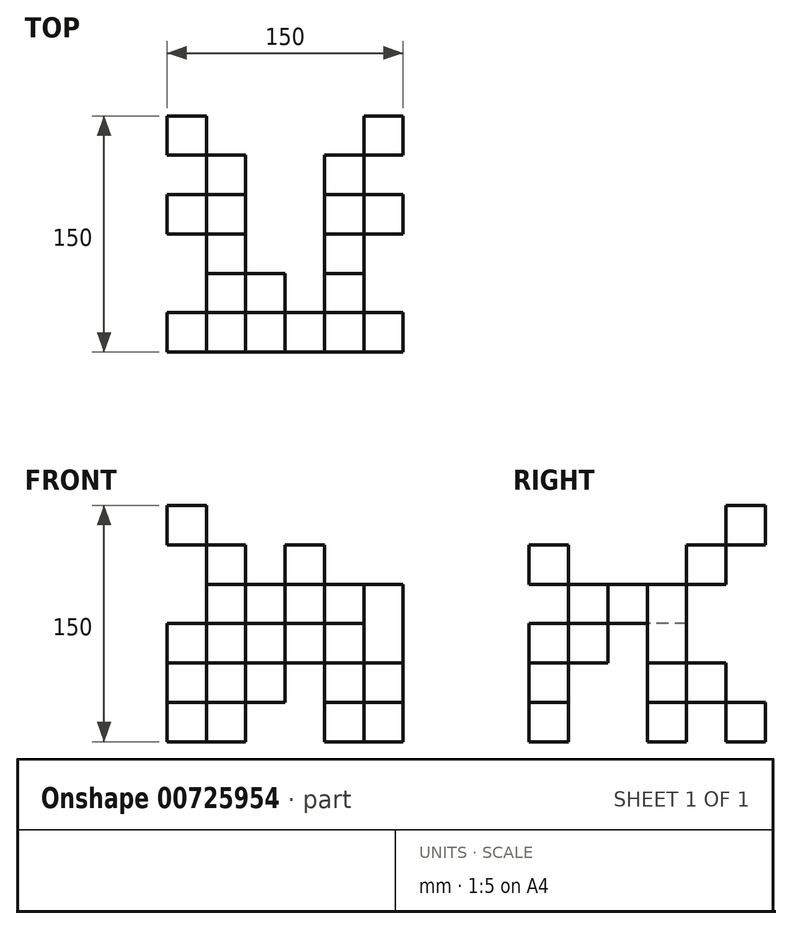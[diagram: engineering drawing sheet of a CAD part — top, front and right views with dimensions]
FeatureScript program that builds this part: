
annotation { "Feature Type Name" : "Feature", "Feature Type Description" : "" }
export const myFeature = defineFeature(function(context is Context, id is Id, definition is map)
    precondition{}
    {
        {
            var Q0;
            Q0=qCreatedBy(makeId("Right.planeOp"),FACE);
            cPlane(context, id + "F0", {"entities" : qUnion([Q0]), "cplaneType" : CPlaneType.OFFSET, "offset" : 25 * mm, "width" : 150 * mm, "height" : 150 * mm});
        }
        {
            var Q0;
            Q0=qCreatedBy(makeId("Right.planeOp"),FACE);
            cPlane(context, id + "F1", {"entities" : qUnion([Q0]), "cplaneType" : CPlaneType.OFFSET, "offset" : 25 * mm, "oppositeDirection" : true, "width" : 150 * mm, "height" : 150 * mm});
        }
        {
            var Q0;
            Q0=qCreatedBy(id+"F1.planeOp",FACE);
            cPlane(context, id + "F2", {"entities" : qUnion([Q0]), "cplaneType" : CPlaneType.OFFSET, "offset" : 25 * mm, "oppositeDirection" : true, "width" : 150 * mm, "height" : 150 * mm});
        }
        {
            var Q0;
            Q0=qCreatedBy(id+"F2.planeOp",FACE);
            cPlane(context, id + "F3", {"entities" : qUnion([Q0]), "cplaneType" : CPlaneType.OFFSET, "offset" : 25 * mm, "oppositeDirection" : true, "width" : 150 * mm, "height" : 150 * mm});
        }
        {
            var Q0;
            Q0=qCreatedBy(makeId("Front.planeOp"),FACE);
            cPlane(context, id + "F4", {"entities" : qUnion([Q0]), "cplaneType" : CPlaneType.OFFSET, "offset" : 25 * mm, "width" : 150 * mm, "height" : 150 * mm});
        }
        {
            var Q0;
            Q0=qCreatedBy(id+"F4.planeOp",FACE);
            cPlane(context, id + "F5", {"entities" : qUnion([Q0]), "cplaneType" : CPlaneType.OFFSET, "offset" : 25 * mm, "width" : 150 * mm, "height" : 150 * mm});
        }
        {
            var Q0;
            Q0=qCreatedBy(makeId("Front.planeOp"),FACE);
            cPlane(context, id + "F6", {"entities" : qUnion([Q0]), "cplaneType" : CPlaneType.OFFSET, "offset" : 25 * mm, "oppositeDirection" : true, "width" : 150 * mm, "height" : 150 * mm});
        }
        {
            var Q0;
            Q0=qCreatedBy(id+"F6.planeOp",FACE);
            cPlane(context, id + "F7", {"entities" : qUnion([Q0]), "cplaneType" : CPlaneType.OFFSET, "offset" : 25 * mm, "oppositeDirection" : true, "width" : 150 * mm, "height" : 150 * mm});
        }
        {
            var Q0;
            Q0=qCreatedBy(makeId("Top.planeOp"),FACE);
            cPlane(context, id + "F8", {"entities" : qUnion([Q0]), "cplaneType" : CPlaneType.OFFSET, "offset" : 25 * mm, "width" : 150 * mm, "height" : 150 * mm});
        }
        {
            var Q0;
            Q0=qCreatedBy(id+"F8.planeOp",FACE);
            cPlane(context, id + "F9", {"entities" : qUnion([Q0]), "cplaneType" : CPlaneType.OFFSET, "offset" : 25 * mm, "width" : 150 * mm, "height" : 150 * mm});
        }
        {
            var Q0;
            Q0=qCreatedBy(makeId("Top.planeOp"),FACE);
            cPlane(context, id + "F10", {"entities" : qUnion([Q0]), "cplaneType" : CPlaneType.OFFSET, "offset" : 25 * mm, "oppositeDirection" : true, "width" : 150 * mm, "height" : 150 * mm});
        }
        {
            var Q0;
            Q0=qCreatedBy(id+"F10.planeOp",FACE);
            cPlane(context, id + "F11", {"entities" : qUnion([Q0]), "cplaneType" : CPlaneType.OFFSET, "offset" : 25 * mm, "oppositeDirection" : true, "width" : 150 * mm, "height" : 150 * mm});
        }
        {
            var Q0;
            Q0=qCreatedBy(id+"F3.planeOp",FACE);
            var sketch = newSketch(context, id + "F12", { "sketchPlane" : qUnion([Q0])});
            skLineSegment(sketch, "E0.bottom", {"start": v(75, -75) * mm, "end": v(50, -75) * mm});
            skLineSegment(sketch, "E0.top", {"start": v(75, -50) * mm, "end": v(50, -50) * mm});
            skLineSegment(sketch, "E0.left", {"start": v(75, -75) * mm, "end": v(75, -50) * mm});
            skLineSegment(sketch, "E0.right", {"start": v(50, -75) * mm, "end": v(50, -50) * mm});
            skSolve(sketch);
        }
        {
            var Q0;
            Q0 = qSketchRegion(id + "F12", true);
            extrude(context, id + "F13", {"entities" : qUnion([Q0]), "depth" : 25 * mm, "offsetDistance" : 25 * mm});
        }
        {
            var Q0;
            Q0=makeQuery(id+"F13.opExtrude","SWEPT_BODY",BODY,{"disambiguationData":[OSD([sQuery(id+"F12.wireOp",EDGE,"E0.bottom"),sQuery(id+"F12.wireOp",EDGE,"E0.top"),sQuery(id+"F12.wireOp",EDGE,"E0.left"),sQuery(id+"F12.wireOp",EDGE,"E0.right")])]});
            transform(context, id + "F14", {"entities" : qUnion([Q0]), "transformType" : TransformType.COPY});
        }
        {
            var Q0;
            Q0=makeQuery(id+"F14.opPattern","COPY",BODY,{"derivedFrom":makeQuery(id+"F13.opExtrude","SWEPT_BODY",BODY,{"disambiguationData":[OSD([sQuery(id+"F12.wireOp",EDGE,"E0.bottom"),sQuery(id+"F12.wireOp",EDGE,"E0.top"),sQuery(id+"F12.wireOp",EDGE,"E0.left"),sQuery(id+"F12.wireOp",EDGE,"E0.right")])]}),"instanceName":"1"});
            transform(context, id + "F15", {"entities" : qUnion([Q0]), "transformType" : TransformType.TRANSLATION_3D, "dx" : 0 * mm, "dy" : -25 * mm, "dz" : 25 * mm, "makeCopy" : true});
        }
        {
            var Q0;
            Q0=makeQuery(id+"F15.opPattern","COPY",BODY,{"derivedFrom":makeQuery(id+"F14.opPattern","COPY",BODY,{"derivedFrom":makeQuery(id+"F13.opExtrude","SWEPT_BODY",BODY,{"disambiguationData":[OSD([sQuery(id+"F12.wireOp",EDGE,"E0.bottom"),sQuery(id+"F12.wireOp",EDGE,"E0.top"),sQuery(id+"F12.wireOp",EDGE,"E0.left"),sQuery(id+"F12.wireOp",EDGE,"E0.right")])]}),"instanceName":"1"}),"instanceName":"1"});
            transform(context, id + "F16", {"entities" : qUnion([Q0]), "transformType" : TransformType.TRANSLATION_3D, "dx" : 0 * mm, "dy" : -25 * mm, "dz" : 25 * mm, "makeCopy" : true});
        }
        {
            var Q0;
            Q0=makeQuery(id+"F15.opPattern","COPY",BODY,{"derivedFrom":makeQuery(id+"F14.opPattern","COPY",BODY,{"derivedFrom":makeQuery(id+"F13.opExtrude","SWEPT_BODY",BODY,{"disambiguationData":[OSD([sQuery(id+"F12.wireOp",EDGE,"E0.bottom"),sQuery(id+"F12.wireOp",EDGE,"E0.top"),sQuery(id+"F12.wireOp",EDGE,"E0.left"),sQuery(id+"F12.wireOp",EDGE,"E0.right")])]}),"instanceName":"1"}),"instanceName":"1"});
            transform(context, id + "F17", {"entities" : qUnion([Q0]), "transformType" : TransformType.TRANSLATION_3D, "dx" : 25 * mm, "dy" : 0 * mm, "dz" : 0 * mm, "makeCopy" : false});
        }
        {
            var Q0;
            Q0=makeQuery(id+"F13.opExtrude","SWEPT_BODY",BODY,{"disambiguationData":[OSD([sQuery(id+"F12.wireOp",EDGE,"E0.bottom"),sQuery(id+"F12.wireOp",EDGE,"E0.top"),sQuery(id+"F12.wireOp",EDGE,"E0.left"),sQuery(id+"F12.wireOp",EDGE,"E0.right")])]});
            var Q1;
            Q1=makeQuery(id+"F16.opPattern","COPY",BODY,{"derivedFrom":makeQuery(id+"F15.opPattern","COPY",BODY,{"derivedFrom":makeQuery(id+"F14.opPattern","COPY",BODY,{"derivedFrom":makeQuery(id+"F13.opExtrude","SWEPT_BODY",BODY,{"disambiguationData":[OSD([sQuery(id+"F12.wireOp",EDGE,"E0.bottom"),sQuery(id+"F12.wireOp",EDGE,"E0.top"),sQuery(id+"F12.wireOp",EDGE,"E0.left"),sQuery(id+"F12.wireOp",EDGE,"E0.right")])]}),"instanceName":"1"}),"instanceName":"1"}),"instanceName":"1"});
            var Q2;
            Q2=makeQuery(id+"F15.opPattern","COPY",BODY,{"derivedFrom":makeQuery(id+"F14.opPattern","COPY",BODY,{"derivedFrom":makeQuery(id+"F13.opExtrude","SWEPT_BODY",BODY,{"disambiguationData":[OSD([sQuery(id+"F12.wireOp",EDGE,"E0.bottom"),sQuery(id+"F12.wireOp",EDGE,"E0.top"),sQuery(id+"F12.wireOp",EDGE,"E0.left"),sQuery(id+"F12.wireOp",EDGE,"E0.right")])]}),"instanceName":"1"}),"instanceName":"1"});
            var Q3;
            Q3=makeQuery(id+"F14.opPattern","COPY",BODY,{"derivedFrom":makeQuery(id+"F13.opExtrude","SWEPT_BODY",BODY,{"disambiguationData":[OSD([sQuery(id+"F12.wireOp",EDGE,"E0.bottom"),sQuery(id+"F12.wireOp",EDGE,"E0.top"),sQuery(id+"F12.wireOp",EDGE,"E0.left"),sQuery(id+"F12.wireOp",EDGE,"E0.right")])]}),"instanceName":"1"});
            var Q4;
            Q4=qCreatedBy(makeId("Front.planeOp"),FACE);
            mirror(context, id + "F18", {"entities" : qUnion([Q0, Q1, Q2, Q3]), "mirrorPlane" : qUnion([Q4])});
        }
        {
            var Q0;
            Q0=makeQuery(id+"F18.opPattern","COPY",BODY,{"derivedFrom":makeQuery(id+"F16.opPattern","COPY",BODY,{"derivedFrom":makeQuery(id+"F15.opPattern","COPY",BODY,{"derivedFrom":makeQuery(id+"F14.opPattern","COPY",BODY,{"derivedFrom":makeQuery(id+"F13.opExtrude","SWEPT_BODY",BODY,{"disambiguationData":[OSD([sQuery(id+"F12.wireOp",EDGE,"E0.bottom"),sQuery(id+"F12.wireOp",EDGE,"E0.top"),sQuery(id+"F12.wireOp",EDGE,"E0.left"),sQuery(id+"F12.wireOp",EDGE,"E0.right")])]}),"instanceName":"1"}),"instanceName":"1"}),"instanceName":"1"}),"instanceName":"1"});
            transform(context, id + "F19", {"entities" : qUnion([Q0]), "transformType" : TransformType.TRANSLATION_3D, "dx" : 0 * mm, "dy" : 0 * mm, "dz" : 25 * mm, "makeCopy" : false});
        }
        {
            var Q0;
            Q0=makeQuery(id+"F18.opPattern","COPY",BODY,{"derivedFrom":makeQuery(id+"F16.opPattern","COPY",BODY,{"derivedFrom":makeQuery(id+"F15.opPattern","COPY",BODY,{"derivedFrom":makeQuery(id+"F14.opPattern","COPY",BODY,{"derivedFrom":makeQuery(id+"F13.opExtrude","SWEPT_BODY",BODY,{"disambiguationData":[OSD([sQuery(id+"F12.wireOp",EDGE,"E0.bottom"),sQuery(id+"F12.wireOp",EDGE,"E0.top"),sQuery(id+"F12.wireOp",EDGE,"E0.left"),sQuery(id+"F12.wireOp",EDGE,"E0.right")])]}),"instanceName":"1"}),"instanceName":"1"}),"instanceName":"1"}),"instanceName":"1"});
            transform(context, id + "F20", {"entities" : qUnion([Q0]), "transformType" : TransformType.TRANSLATION_3D, "dx" : 25 * mm, "dy" : 0 * mm, "dz" : 0 * mm, "makeCopy" : false});
        }
        {
            var Q0;
            Q0=makeQuery(id+"F18.opPattern","COPY",BODY,{"derivedFrom":makeQuery(id+"F15.opPattern","COPY",BODY,{"derivedFrom":makeQuery(id+"F14.opPattern","COPY",BODY,{"derivedFrom":makeQuery(id+"F13.opExtrude","SWEPT_BODY",BODY,{"disambiguationData":[OSD([sQuery(id+"F12.wireOp",EDGE,"E0.bottom"),sQuery(id+"F12.wireOp",EDGE,"E0.top"),sQuery(id+"F12.wireOp",EDGE,"E0.left"),sQuery(id+"F12.wireOp",EDGE,"E0.right")])]}),"instanceName":"1"}),"instanceName":"1"}),"instanceName":"1"});
            var Q1;
            Q1=makeQuery(id+"F18.opPattern","COPY",BODY,{"derivedFrom":makeQuery(id+"F13.opExtrude","SWEPT_BODY",BODY,{"disambiguationData":[OSD([sQuery(id+"F12.wireOp",EDGE,"E0.bottom"),sQuery(id+"F12.wireOp",EDGE,"E0.top"),sQuery(id+"F12.wireOp",EDGE,"E0.left"),sQuery(id+"F12.wireOp",EDGE,"E0.right")])]}),"instanceName":"1"});
            transform(context, id + "F21", {"entities" : qUnion([Q0, Q1]), "transformType" : TransformType.TRANSLATION_3D, "dx" : 0 * mm, "dy" : 0 * mm, "dz" : 25 * mm, "makeCopy" : false});
        }
        {
            var Q0;
            Q0=makeQuery(id+"F18.opPattern","COPY",BODY,{"derivedFrom":makeQuery(id+"F14.opPattern","COPY",BODY,{"derivedFrom":makeQuery(id+"F13.opExtrude","SWEPT_BODY",BODY,{"disambiguationData":[OSD([sQuery(id+"F12.wireOp",EDGE,"E0.bottom"),sQuery(id+"F12.wireOp",EDGE,"E0.top"),sQuery(id+"F12.wireOp",EDGE,"E0.left"),sQuery(id+"F12.wireOp",EDGE,"E0.right")])]}),"instanceName":"1"}),"instanceName":"1"});
            transform(context, id + "F22", {"entities" : qUnion([Q0]), "transformType" : TransformType.TRANSLATION_3D, "dx" : 25 * mm, "dy" : 0 * mm, "dz" : 0 * mm, "makeCopy" : false});
        }
        {
            var Q0;
            Q0=makeQuery(id+"F13.opExtrude","SWEPT_BODY",BODY,{"disambiguationData":[OSD([sQuery(id+"F12.wireOp",EDGE,"E0.bottom"),sQuery(id+"F12.wireOp",EDGE,"E0.top"),sQuery(id+"F12.wireOp",EDGE,"E0.left"),sQuery(id+"F12.wireOp",EDGE,"E0.right")])]});
            var Q1;
            Q1=makeQuery(id+"F18.opPattern","COPY",BODY,{"derivedFrom":makeQuery(id+"F16.opPattern","COPY",BODY,{"derivedFrom":makeQuery(id+"F15.opPattern","COPY",BODY,{"derivedFrom":makeQuery(id+"F14.opPattern","COPY",BODY,{"derivedFrom":makeQuery(id+"F13.opExtrude","SWEPT_BODY",BODY,{"disambiguationData":[OSD([sQuery(id+"F12.wireOp",EDGE,"E0.bottom"),sQuery(id+"F12.wireOp",EDGE,"E0.top"),sQuery(id+"F12.wireOp",EDGE,"E0.left"),sQuery(id+"F12.wireOp",EDGE,"E0.right")])]}),"instanceName":"1"}),"instanceName":"1"}),"instanceName":"1"}),"instanceName":"1"});
            var Q2;
            Q2=makeQuery(id+"F18.opPattern","COPY",BODY,{"derivedFrom":makeQuery(id+"F14.opPattern","COPY",BODY,{"derivedFrom":makeQuery(id+"F13.opExtrude","SWEPT_BODY",BODY,{"disambiguationData":[OSD([sQuery(id+"F12.wireOp",EDGE,"E0.bottom"),sQuery(id+"F12.wireOp",EDGE,"E0.top"),sQuery(id+"F12.wireOp",EDGE,"E0.left"),sQuery(id+"F12.wireOp",EDGE,"E0.right")])]}),"instanceName":"1"}),"instanceName":"1"});
            var Q3;
            Q3=makeQuery(id+"F18.opPattern","COPY",BODY,{"derivedFrom":makeQuery(id+"F15.opPattern","COPY",BODY,{"derivedFrom":makeQuery(id+"F14.opPattern","COPY",BODY,{"derivedFrom":makeQuery(id+"F13.opExtrude","SWEPT_BODY",BODY,{"disambiguationData":[OSD([sQuery(id+"F12.wireOp",EDGE,"E0.bottom"),sQuery(id+"F12.wireOp",EDGE,"E0.top"),sQuery(id+"F12.wireOp",EDGE,"E0.left"),sQuery(id+"F12.wireOp",EDGE,"E0.right")])]}),"instanceName":"1"}),"instanceName":"1"}),"instanceName":"1"});
            var Q4;
            Q4=makeQuery(id+"F16.opPattern","COPY",BODY,{"derivedFrom":makeQuery(id+"F15.opPattern","COPY",BODY,{"derivedFrom":makeQuery(id+"F14.opPattern","COPY",BODY,{"derivedFrom":makeQuery(id+"F13.opExtrude","SWEPT_BODY",BODY,{"disambiguationData":[OSD([sQuery(id+"F12.wireOp",EDGE,"E0.bottom"),sQuery(id+"F12.wireOp",EDGE,"E0.top"),sQuery(id+"F12.wireOp",EDGE,"E0.left"),sQuery(id+"F12.wireOp",EDGE,"E0.right")])]}),"instanceName":"1"}),"instanceName":"1"}),"instanceName":"1"});
            var Q5;
            Q5=makeQuery(id+"F15.opPattern","COPY",BODY,{"derivedFrom":makeQuery(id+"F14.opPattern","COPY",BODY,{"derivedFrom":makeQuery(id+"F13.opExtrude","SWEPT_BODY",BODY,{"disambiguationData":[OSD([sQuery(id+"F12.wireOp",EDGE,"E0.bottom"),sQuery(id+"F12.wireOp",EDGE,"E0.top"),sQuery(id+"F12.wireOp",EDGE,"E0.left"),sQuery(id+"F12.wireOp",EDGE,"E0.right")])]}),"instanceName":"1"}),"instanceName":"1"});
            var Q6;
            Q6=makeQuery(id+"F18.opPattern","COPY",BODY,{"derivedFrom":makeQuery(id+"F13.opExtrude","SWEPT_BODY",BODY,{"disambiguationData":[OSD([sQuery(id+"F12.wireOp",EDGE,"E0.bottom"),sQuery(id+"F12.wireOp",EDGE,"E0.top"),sQuery(id+"F12.wireOp",EDGE,"E0.left"),sQuery(id+"F12.wireOp",EDGE,"E0.right")])]}),"instanceName":"1"});
            var Q7;
            Q7=makeQuery(id+"F14.opPattern","COPY",BODY,{"derivedFrom":makeQuery(id+"F13.opExtrude","SWEPT_BODY",BODY,{"disambiguationData":[OSD([sQuery(id+"F12.wireOp",EDGE,"E0.bottom"),sQuery(id+"F12.wireOp",EDGE,"E0.top"),sQuery(id+"F12.wireOp",EDGE,"E0.left"),sQuery(id+"F12.wireOp",EDGE,"E0.right")])]}),"instanceName":"1"});
            var Q8;
            Q8=qCreatedBy(makeId("Right.planeOp"),FACE);
            mirror(context, id + "F23", {"entities" : qUnion([Q0, Q1, Q2, Q3, Q4, Q5, Q6, Q7]), "mirrorPlane" : qUnion([Q8])});
        }
        {
            var Q0;
            Q0=makeQuery(id+"F23.opPattern","COPY",BODY,{"derivedFrom":makeQuery(id+"F18.opPattern","COPY",BODY,{"derivedFrom":makeQuery(id+"F13.opExtrude","SWEPT_BODY",BODY,{"disambiguationData":[OSD([sQuery(id+"F12.wireOp",EDGE,"E0.bottom"),sQuery(id+"F12.wireOp",EDGE,"E0.top"),sQuery(id+"F12.wireOp",EDGE,"E0.left"),sQuery(id+"F12.wireOp",EDGE,"E0.right")])]}),"instanceName":"1"}),"instanceName":"1"});
            var Q1;
            Q1=makeQuery(id+"F23.opPattern","COPY",BODY,{"derivedFrom":makeQuery(id+"F18.opPattern","COPY",BODY,{"derivedFrom":makeQuery(id+"F14.opPattern","COPY",BODY,{"derivedFrom":makeQuery(id+"F13.opExtrude","SWEPT_BODY",BODY,{"disambiguationData":[OSD([sQuery(id+"F12.wireOp",EDGE,"E0.bottom"),sQuery(id+"F12.wireOp",EDGE,"E0.top"),sQuery(id+"F12.wireOp",EDGE,"E0.left"),sQuery(id+"F12.wireOp",EDGE,"E0.right")])]}),"instanceName":"1"}),"instanceName":"1"}),"instanceName":"1"});
            transform(context, id + "F24", {"entities" : qUnion([Q0, Q1]), "transformType" : TransformType.TRANSLATION_3D, "dx" : -50 * mm, "dy" : 0 * mm, "dz" : 25 * mm, "makeCopy" : true});
        }
        {
            var Q0;
            Q0=makeQuery(id+"F24.opPattern","COPY",BODY,{"derivedFrom":makeQuery(id+"F23.opPattern","COPY",BODY,{"derivedFrom":makeQuery(id+"F18.opPattern","COPY",BODY,{"derivedFrom":makeQuery(id+"F13.opExtrude","SWEPT_BODY",BODY,{"disambiguationData":[OSD([sQuery(id+"F12.wireOp",EDGE,"E0.bottom"),sQuery(id+"F12.wireOp",EDGE,"E0.top"),sQuery(id+"F12.wireOp",EDGE,"E0.left"),sQuery(id+"F12.wireOp",EDGE,"E0.right")])]}),"instanceName":"1"}),"instanceName":"1"}),"instanceName":"1"});
            var Q1;
            Q1=makeQuery(id+"F24.opPattern","COPY",BODY,{"derivedFrom":makeQuery(id+"F23.opPattern","COPY",BODY,{"derivedFrom":makeQuery(id+"F18.opPattern","COPY",BODY,{"derivedFrom":makeQuery(id+"F14.opPattern","COPY",BODY,{"derivedFrom":makeQuery(id+"F13.opExtrude","SWEPT_BODY",BODY,{"disambiguationData":[OSD([sQuery(id+"F12.wireOp",EDGE,"E0.bottom"),sQuery(id+"F12.wireOp",EDGE,"E0.top"),sQuery(id+"F12.wireOp",EDGE,"E0.left"),sQuery(id+"F12.wireOp",EDGE,"E0.right")])]}),"instanceName":"1"}),"instanceName":"1"}),"instanceName":"1"}),"instanceName":"1"});
            transform(context, id + "F25", {"entities" : qUnion([Q0, Q1]), "transformType" : TransformType.TRANSLATION_3D, "dx" : 0 * mm, "dy" : 0 * mm, "dz" : 50 * mm, "makeCopy" : true});
        }
        {
            var Q0;
            Q0=makeQuery(id+"F25.opPattern","COPY",BODY,{"derivedFrom":makeQuery(id+"F24.opPattern","COPY",BODY,{"derivedFrom":makeQuery(id+"F23.opPattern","COPY",BODY,{"derivedFrom":makeQuery(id+"F18.opPattern","COPY",BODY,{"derivedFrom":makeQuery(id+"F14.opPattern","COPY",BODY,{"derivedFrom":makeQuery(id+"F13.opExtrude","SWEPT_BODY",BODY,{"disambiguationData":[OSD([sQuery(id+"F12.wireOp",EDGE,"E0.bottom"),sQuery(id+"F12.wireOp",EDGE,"E0.top"),sQuery(id+"F12.wireOp",EDGE,"E0.left"),sQuery(id+"F12.wireOp",EDGE,"E0.right")])]}),"instanceName":"1"}),"instanceName":"1"}),"instanceName":"1"}),"instanceName":"1"}),"instanceName":"1"});
            transform(context, id + "F26", {"entities" : qUnion([Q0]), "transformType" : TransformType.TRANSLATION_3D, "dx" : 0 * mm, "dy" : 25 * mm, "dz" : 0 * mm, "makeCopy" : false});
        }
        {
            var Q0;
            Q0=makeQuery(id+"F15.opPattern","COPY",BODY,{"derivedFrom":makeQuery(id+"F14.opPattern","COPY",BODY,{"derivedFrom":makeQuery(id+"F13.opExtrude","SWEPT_BODY",BODY,{"disambiguationData":[OSD([sQuery(id+"F12.wireOp",EDGE,"E0.bottom"),sQuery(id+"F12.wireOp",EDGE,"E0.top"),sQuery(id+"F12.wireOp",EDGE,"E0.left"),sQuery(id+"F12.wireOp",EDGE,"E0.right")])]}),"instanceName":"1"}),"instanceName":"1"});
            var Q1;
            Q1=makeQuery(id+"F13.opExtrude","SWEPT_BODY",BODY,{"disambiguationData":[OSD([sQuery(id+"F12.wireOp",EDGE,"E0.bottom"),sQuery(id+"F12.wireOp",EDGE,"E0.top"),sQuery(id+"F12.wireOp",EDGE,"E0.left"),sQuery(id+"F12.wireOp",EDGE,"E0.right")])]});
            var Q2;
            Q2=makeQuery(id+"F23.opPattern","COPY",BODY,{"derivedFrom":makeQuery(id+"F16.opPattern","COPY",BODY,{"derivedFrom":makeQuery(id+"F15.opPattern","COPY",BODY,{"derivedFrom":makeQuery(id+"F14.opPattern","COPY",BODY,{"derivedFrom":makeQuery(id+"F13.opExtrude","SWEPT_BODY",BODY,{"disambiguationData":[OSD([sQuery(id+"F12.wireOp",EDGE,"E0.bottom"),sQuery(id+"F12.wireOp",EDGE,"E0.top"),sQuery(id+"F12.wireOp",EDGE,"E0.left"),sQuery(id+"F12.wireOp",EDGE,"E0.right")])]}),"instanceName":"1"}),"instanceName":"1"}),"instanceName":"1"}),"instanceName":"1"});
            var Q3;
            Q3=qCreatedBy(makeId("Top.planeOp"),FACE);
            mirror(context, id + "F27", {"operationType" : NewBodyOperationType.ADD, "entities" : qUnion([Q0, Q1, Q2]), "mirrorPlane" : qUnion([Q3])});
        }
        {
            var Q0;
            Q0=makeQuery(id+"F18.opPattern","COPY",BODY,{"derivedFrom":makeQuery(id+"F13.opExtrude","SWEPT_BODY",BODY,{"disambiguationData":[OSD([sQuery(id+"F12.wireOp",EDGE,"E0.bottom"),sQuery(id+"F12.wireOp",EDGE,"E0.top"),sQuery(id+"F12.wireOp",EDGE,"E0.left"),sQuery(id+"F12.wireOp",EDGE,"E0.right")])]}),"instanceName":"1"});
            var Q1;
            Q1=makeQuery(id+"F18.opPattern","COPY",BODY,{"derivedFrom":makeQuery(id+"F14.opPattern","COPY",BODY,{"derivedFrom":makeQuery(id+"F13.opExtrude","SWEPT_BODY",BODY,{"disambiguationData":[OSD([sQuery(id+"F12.wireOp",EDGE,"E0.bottom"),sQuery(id+"F12.wireOp",EDGE,"E0.top"),sQuery(id+"F12.wireOp",EDGE,"E0.left"),sQuery(id+"F12.wireOp",EDGE,"E0.right")])]}),"instanceName":"1"}),"instanceName":"1"});
            var Q2;
            Q2=makeQuery(id+"F23.opPattern","COPY",BODY,{"derivedFrom":makeQuery(id+"F18.opPattern","COPY",BODY,{"derivedFrom":makeQuery(id+"F14.opPattern","COPY",BODY,{"derivedFrom":makeQuery(id+"F13.opExtrude","SWEPT_BODY",BODY,{"disambiguationData":[OSD([sQuery(id+"F12.wireOp",EDGE,"E0.bottom"),sQuery(id+"F12.wireOp",EDGE,"E0.top"),sQuery(id+"F12.wireOp",EDGE,"E0.left"),sQuery(id+"F12.wireOp",EDGE,"E0.right")])]}),"instanceName":"1"}),"instanceName":"1"}),"instanceName":"1"});
            var Q3;
            Q3=qCreatedBy(id+"F4.planeOp",FACE);
            mirror(context, id + "F28", {"operationType" : NewBodyOperationType.ADD, "entities" : qUnion([Q0, Q1, Q2]), "mirrorPlane" : qUnion([Q3])});
        }
    });
